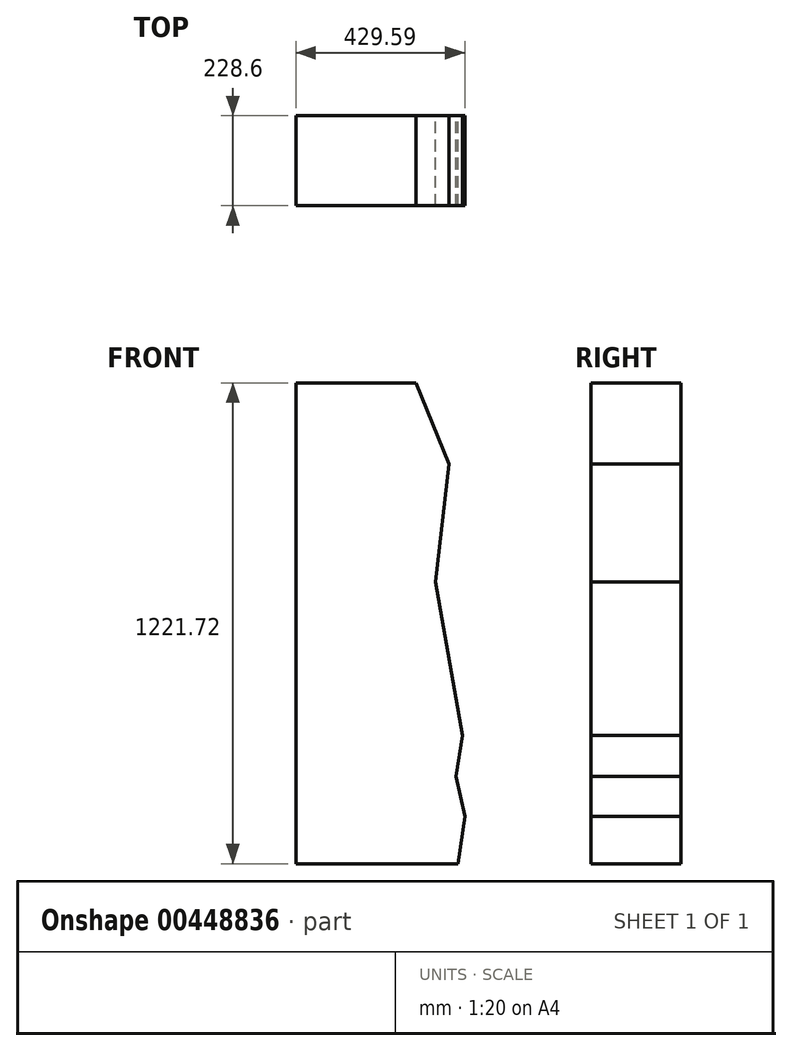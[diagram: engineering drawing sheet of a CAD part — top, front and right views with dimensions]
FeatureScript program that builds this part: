
annotation { "Feature Type Name" : "Feature", "Feature Type Description" : "" }
export const myFeature = defineFeature(function(context is Context, id is Id, definition is map)
    precondition{}
    {
        {
            var Q0;
            Q0=qCreatedBy(makeId("Front.planeOp"),FACE);
            var sketch = newSketch(context, id + "F0", { "sketchPlane" : qUnion([Q0])});
            skLineSegment(sketch, "E0", {"start": v(-654.63, 607.37) * mm, "end": v(-654.63, -614.35) * mm});
            skLineSegment(sketch, "E1", {"start": v(-654.63, -614.35) * mm, "end": v(-243.25, -614.35) * mm});
            skLineSegment(sketch, "E2", {"start": v(-243.25, -614.35) * mm, "end": v(-225.04, -494.47) * mm});
            skLineSegment(sketch, "E3", {"start": v(-225.04, -494.47) * mm, "end": v(-247.99, -391.89) * mm});
            skLineSegment(sketch, "E4", {"start": v(-247.99, -391.89) * mm, "end": v(-231.79, -287.96) * mm});
            skLineSegment(sketch, "E5", {"start": v(-231.79, -287.96) * mm, "end": v(-299.27, 100.94) * mm});
            skLineSegment(sketch, "E6", {"start": v(-299.27, 100.94) * mm, "end": v(-265.53, 401.21) * mm});
            skPoint(sketch, "E6.endSnap0", {"position": v(-265.53, -93.5) * mm});
            skLineSegment(sketch, "E7", {"start": v(-265.53, 401.21) * mm, "end": v(-349.83, 607.37) * mm});
            skLineSegment(sketch, "E8", {"start": v(-349.83, 607.37) * mm, "end": v(-654.63, 607.37) * mm});
            skLineSegment(sketch, "E9", {"start": v(-332.39, 690.58) * mm, "end": v(-209.8, 370.34) * mm});
            skLineSegment(sketch, "E10", {"start": v(-209.8, 370.34) * mm, "end": v(-241.58, 81.83) * mm});
            skLineSegment(sketch, "E11", {"start": v(-241.58, 81.83) * mm, "end": v(-168.2, -298.44) * mm});
            skLineSegment(sketch, "E12", {"start": v(-168.2, -298.44) * mm, "end": v(-202.26, -405.22) * mm});
            skLineSegment(sketch, "E13", {"start": v(-202.26, -405.22) * mm, "end": v(-168.2, -516.52) * mm});
            skLineSegment(sketch, "E14", {"start": v(-168.2, -516.52) * mm, "end": v(-215.74, -682.93) * mm});
            skLineSegment(sketch, "E15", {"start": v(-215.74, -682.93) * mm, "end": v(326.13, -682.93) * mm});
            skLineSegment(sketch, "E16", {"start": v(326.13, -682.93) * mm, "end": v(326.13, 81.83) * mm});
            skLineSegment(sketch, "E17", {"start": v(326.13, 81.83) * mm, "end": v(269.57, 379.74) * mm});
            skLineSegment(sketch, "E18", {"start": v(269.57, 379.74) * mm, "end": v(324.71, 536.69) * mm});
            skLineSegment(sketch, "E19", {"start": v(324.71, 536.69) * mm, "end": v(277.21, 690.58) * mm});
            skLineSegment(sketch, "E20", {"start": v(-332.39, 690.58) * mm, "end": v(277.21, 690.58) * mm});
            skLineSegment(sketch, "E21", {"start": v(1676, 190.04) * mm, "end": v(1619.46, 487.95) * mm});
            skLineSegment(sketch, "E22", {"start": v(1619.46, 487.95) * mm, "end": v(1674.6, 644.9) * mm});
            skLineSegment(sketch, "E23", {"start": v(1674.6, 644.9) * mm, "end": v(1627.1, 798.79) * mm});
            skLineSegment(sketch, "E24", {"start": v(1676, 190.04) * mm, "end": v(1676, -309.7) * mm});
            skLineSegment(sketch, "E25", {"start": v(1676, -309.7) * mm, "end": v(2032.05, -309.7) * mm});
            skLineSegment(sketch, "E26", {"start": v(2032.05, -309.7) * mm, "end": v(2032.05, 798.79) * mm});
            skLineSegment(sketch, "E27", {"start": v(2032.05, 798.79) * mm, "end": v(1627.1, 798.79) * mm});
            skLineSegment(sketch, "E28", {"start": v(2230.78, -204.62) * mm, "end": v(2032.05, -204.62) * mm});
            skLineSegment(sketch, "E29", {"start": v(-879.39, 226.5) * mm, "end": v(-654.63, 226.5) * mm});
            skLineSegment(sketch, "E30", {"start": v(2153.8, 226.5) * mm, "end": v(2174.33, 164.9) * mm});
            skLineSegment(sketch, "E31", {"start": v(2174.33, 164.9) * mm, "end": v(2174.33, 54.56) * mm});
            skLineSegment(sketch, "E32", {"start": v(2174.33, 54.56) * mm, "end": v(2205.12, 0) * mm});
            skLineSegment(sketch, "E33", {"start": v(2205.12, 0) * mm, "end": v(2179.46, -104.54) * mm});
            skLineSegment(sketch, "E34", {"start": v(2179.46, -104.54) * mm, "end": v(2230.78, -163.56) * mm});
            skLineSegment(sketch, "E35", {"start": v(2230.78, -163.56) * mm, "end": v(2230.78, -204.62) * mm});
            skLineSegment(sketch, "E36", {"start": v(-879.39, 226.5) * mm, "end": v(-879.39, 171.17) * mm});
            skLineSegment(sketch, "E37", {"start": v(-879.39, 171.17) * mm, "end": v(-834.58, 76.57) * mm});
            skLineSegment(sketch, "E38", {"start": v(-834.58, 76.57) * mm, "end": v(-834.58, 0) * mm});
            skLineSegment(sketch, "E39", {"start": v(-834.58, 0) * mm, "end": v(-879.39, -97.38) * mm});
            skLineSegment(sketch, "E40", {"start": v(-879.39, -97.38) * mm, "end": v(-879.39, -161.47) * mm});
            skLineSegment(sketch, "E41", {"start": v(-879.39, -161.47) * mm, "end": v(-828.06, -204.62) * mm});
            skLineSegment(sketch, "E42.trimOffspring", {"start": v(298.66, 226.5) * mm, "end": v(1669.09, 226.5) * mm});
            skLineSegment(sketch, "E43.trimOffspring", {"start": v(-186.3, -204.62) * mm, "end": v(-246.25, -204.62) * mm});
            skLineSegment(sketch, "E44.trimOffspring", {"start": v(-285.17, 226.5) * mm, "end": v(-225.64, 226.5) * mm});
            skLineSegment(sketch, "E45.trimOffspring", {"start": v(-654.63, -204.62) * mm, "end": v(-828.06, -204.62) * mm});
            skLineSegment(sketch, "E46.trimOffspring", {"start": v(2032.05, 226.5) * mm, "end": v(2153.8, 226.5) * mm});
            skLineSegment(sketch, "E47.trimOffspring", {"start": v(1676, -204.62) * mm, "end": v(326.13, -204.62) * mm});
            skSolve(sketch);
        }
        {
            var Q0;
            {var subQ10=sQuery(id+"F0.wireOp",EDGE,"E1");Q0=makeQuery(id+"F0.imprint","IMPRINT",FACE,{"disambiguationData":[TD([[makeQuery(id+"F0.imprint","IMPRINT",EDGE,{"derivedFrom":subQ10}),1.0]])]});}
            extrude(context, id + "F1", {"entities" : qUnion([Q0]), "depth" : 228.6 * mm});
        }
    });
